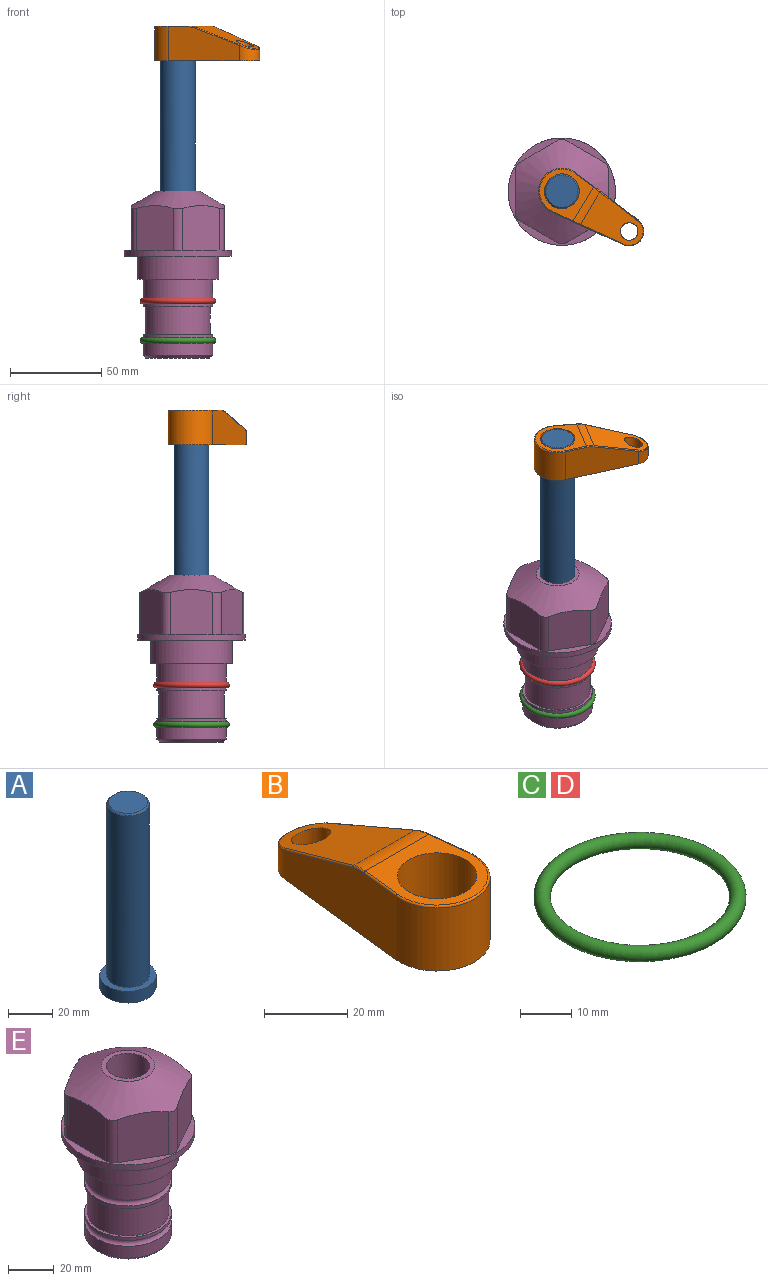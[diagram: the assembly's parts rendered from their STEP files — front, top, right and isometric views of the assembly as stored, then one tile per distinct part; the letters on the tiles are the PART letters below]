
ASSEMBLY  parts=5 mates=3
PART A: 6 faces, bbox 25.4x25.4x101.6 mm
  f0: plane 17.46x17.46mm, normal (0,0,1), area 239.5mm2, adj f5
  f1: plane 25.4x25.4mm, normal (0,0,-1), area 506.7mm2, adj f2
  f2: cylinder r=12.7mm len=25.4mm, axis (0,0,1), area 506.7mm2, adj f1,f3
  f3: plane 25.4x25.4mm, normal (0,0,1), area 221.7mm2, adj f2,f4
  f4: cylinder r=9.53mm len=94.46mm, axis (0,0,1), area 5653mm2, adj f3,f5
  f5: cone r=8.73mm half-angle=45deg, axis (0,0,-1), area 64.4mm2, adj f0,f4
PART B: 44 faces, bbox 27.5x64.5x19.1 mm
  f0: plane 2.3x0.95mm, normal (0,0,-1), area 1mm2, adj f25,f30,f34
  f1: plane 63.5x25.4mm, normal (0,0,-1), area 561.7mm2, adj f2,f3,f4,f5,f6,f7,f19,f20
  f2: cylinder r=12.7mm len=25.4mm, axis (0,0,-1), area 792.2mm2, adj f1,f3,f5,f13
  f3: plane 42.33x18.54mm, normal (0.99,0.11,0), area 647mm2, adj f1,f2,f4,f11,f12,f14
  f4: cylinder r=7.94mm len=15.78mm, axis (0,0,-1), area 158.6mm2, adj f1,f3,f5,f16
  f5: plane 42.33x18.54mm, normal (-0.99,0.11,0), area 647mm2, adj f1,f2,f4,f15,f17,f18
  f6: cylinder r=9.53mm len=19.05mm, axis (0,0,-1), area 1140.1mm2, adj f1,f8
  f7: cylinder r=4.76mm len=10.98mm, axis (0,0,-1), area 276.1mm2, adj f1,f9
  f8: plane 25.83x24.38mm, normal (0,0,1), area 262.2mm2, adj f6,f10,f11,f13,f15
  f9: plane 32.49x20.55mm, normal (0,0.34,0.94), area 489.9mm2, adj f7,f10,f14,f16,f18
  f10: cylinder r=12.7mm len=21.49mm, axis (-1,0,0), area 93.2mm2, adj f8,f9,f12,f17
  f11: cylinder r=0.51mm len=12.34mm, axis (0.11,-0.99,0), area 9.9mm2, adj f3,f8,f12,f13
  f12: bspline ~7.62x1.64mm, area 3.5mm2, adj f3,f10,f11,f14
  f13: torus R=12.19mm, axis (0,0,1), area 33.6mm2, adj f2,f8,f11,f15
  f14: cylinder r=0.51mm len=26.01mm, axis (0.1,-0.93,0.34), area 21.6mm2, adj f3,f9,f12,f16
  f15: cylinder r=0.51mm len=12.34mm, axis (0.11,0.99,0), area 9.9mm2, adj f5,f8,f13,f17
  f16: bspline ~15.78x7.05mm, area 15.7mm2, adj f4,f9,f14,f18
  f17: bspline ~7.62x1.64mm, area 3.5mm2, adj f5,f10,f15,f18
  f18: cylinder r=0.51mm len=26.01mm, axis (0.1,0.93,-0.34), area 21.6mm2, adj f5,f9,f16,f17
  f19: plane 21.6x14.29mm, normal (-0.99,-0.11,0), area 242.6mm2, adj f1,f26,f28,f34,f36,f38
  f20: plane 21.6x14.29mm, normal (0.99,-0.11,0), area 242.6mm2, adj f1,f27,f29,f37,f39,f41
  f21: cylinder r=12.7mm len=14.29mm, axis (0,0,-1), area 173.2mm2, adj f1,f26,f27,f30,f31,f33
  f22: cylinder r=7.94mm len=7.63mm, axis (0,0,-1), area 53.8mm2, adj f1,f28,f29,f42
  f23: plane 2.3x0.95mm, normal (0,0,-1), area 1mm2, adj f25,f33,f37
  f24: plane 17.94x12.32mm, normal (0,-0.34,-0.94), area 191.2mm2, adj f25,f38,f41,f42
  f25: cylinder r=9.53mm len=12.93mm, axis (-1,0,0), area 37.5mm2, adj f0,f23,f24,f31,f36,f39
  f26: cylinder r=1.59mm len=14.29mm, axis (0,0,-1), area 49mm2, adj f1,f19,f21,f32
  f27: cylinder r=1.59mm len=14.29mm, axis (0,0,-1), area 49mm2, adj f1,f20,f21,f35
  f28: cylinder r=1.59mm len=7.28mm, axis (0,0,-1), area 22.1mm2, adj f1,f19,f22,f40
  f29: cylinder r=1.59mm len=7.28mm, axis (0,0,-1), area 22.1mm2, adj f1,f20,f22,f43
  f30: torus R=14.29mm, axis (0,0,1), area 5.8mm2, adj f0,f21,f31,f32
  f31: bspline ~11.06x2.73mm, area 20.8mm2, adj f21,f25,f30,f33
  f32: sphere r=1.59mm, area 5.4mm2, adj f26,f30,f34
  f33: torus R=14.29mm, axis (0,0,1), area 5.8mm2, adj f21,f23,f31,f35
  f34: cylinder r=1.59mm len=1.68mm, axis (-0.11,0.99,0), area 2.4mm2, adj f0,f19,f32,f36
  f35: sphere r=1.59mm, area 5.4mm2, adj f27,f33,f37
  f36: bspline ~5.82x2.33mm, area 7.7mm2, adj f19,f25,f34,f38
  f37: cylinder r=1.59mm len=1.68mm, axis (0.11,0.99,0), area 2.4mm2, adj f20,f23,f35,f39
  f38: cylinder r=1.59mm len=18.33mm, axis (0.1,-0.93,0.34), area 46.7mm2, adj f19,f24,f36,f40
  f39: bspline ~5.82x2.33mm, area 7.7mm2, adj f20,f25,f37,f41
  f40: sphere r=1.59mm, area 3.6mm2, adj f28,f38,f42
  f41: cylinder r=1.59mm len=18.33mm, axis (0.1,0.93,-0.34), area 46.7mm2, adj f20,f24,f39,f43
  f42: bspline ~8.31x1.84mm, area 15.3mm2, adj f22,f24,f40,f43
  f43: sphere r=1.59mm, area 3.6mm2, adj f29,f41,f42
PART C: 1 faces, bbox 44.7x44.7x3.2 mm
  f0: torus R=19.05mm, axis (0,0,1), area 1193.9mm2
PART D: same geometry as C
PART E: 36 faces, bbox 58.7x58.7x91.2 mm
  f0: cylinder r=17.78mm len=35.56mm, axis (0,0,1), area 1670.8mm2, adj f23,f24,f31
  f1: cylinder r=19.05mm len=38.1mm, axis (0,0,1), area 1191.9mm2, adj f26,f27,f30
  f2: plane 58.66x58.66mm, normal (0,0,-1), area 1150.6mm2, adj f3,f28
  f3: cylinder r=29.33mm len=58.66mm, axis (0,0,-1), area 585.1mm2, adj f2,f4
  f4: plane 58.66x58.66mm, normal (0,0,1), area 475.9mm2, adj f3,f5,f6,f7,f8,f9,f10,f11
  f5: plane 24.5x20.32mm, normal (-0.5,0.87,0), area 562.8mm2, adj f4,f15,f16,f17
  f6: plane 24.5x20.32mm, normal (0.5,0.87,0), area 562.8mm2, adj f4,f14,f15,f17
  f7: plane 24.5x23.48mm, normal (1,0,0), area 562.8mm2, adj f4,f13,f14,f17
  f8: plane 24.5x20.32mm, normal (0.5,-0.87,0), area 562.8mm2, adj f4,f12,f13,f17
  f9: plane 24.5x20.32mm, normal (-0.5,-0.87,0), area 562.8mm2, adj f4,f11,f12,f17
  f10: plane 24.5x23.48mm, normal (-1,0,0), area 562.8mm2, adj f4,f11,f16,f17
  f11: cylinder r=5.08mm len=23.01mm, axis (0,0,-1), area 121.2mm2, adj f4,f9,f10,f17
  f12: cylinder r=5.08mm len=23.01mm, axis (0,0,-1), area 121.2mm2, adj f4,f8,f9,f17
  f13: cylinder r=5.08mm len=23.01mm, axis (0,0,-1), area 121.2mm2, adj f4,f7,f8,f17
  f14: cylinder r=5.08mm len=23.01mm, axis (0,0,-1), area 121.2mm2, adj f4,f6,f7,f17
  f15: cylinder r=5.08mm len=23.01mm, axis (0,0,-1), area 121.2mm2, adj f4,f5,f6,f17
  f16: cylinder r=5.08mm len=23.01mm, axis (0,0,-1), area 121.2mm2, adj f4,f5,f10,f17
  f17: cone r=11.73mm half-angle=60deg, axis (0,0,-1), area 2071.8mm2, adj f5,f6,f7,f8,f9,f10,f11,f12
  f18: plane 23.46x23.46mm, normal (0,0,1), area 147.4mm2, adj f17,f35
  f19: plane 34.93x34.93mm, normal (0,0,-1), area 958mm2, adj f29
  f20: cylinder r=19.05mm len=38.1mm, axis (0,0,1), area 760.1mm2, adj f21,f29
  f21: torus R=19.05mm, axis (0,0,1), area 565.3mm2, adj f20,f22
  f22: cylinder r=19.05mm len=38.1mm, axis (0,0,1), area 190mm2, adj f21,f23
  f23: plane 38.1x38.1mm, normal (0,0,1), area 146.9mm2, adj f0,f22
  f24: plane 38.1x38.1mm, normal (0,0,-1), area 146.9mm2, adj f0,f25
  f25: cylinder r=19.05mm len=38.1mm, axis (0,0,1), area 190mm2, adj f24,f26
  f26: torus R=19.05mm, axis (0,0,1), area 565.3mm2, adj f1,f25
  f27: plane 44.45x44.45mm, normal (0,0,-1), area 411.7mm2, adj f1,f28
  f28: cylinder r=22.23mm len=44.45mm, axis (0,0,1), area 1773.5mm2, adj f2,f27
  f29: cone r=19.05mm half-angle=45deg, axis (0,0,1), area 257.5mm2, adj f19,f20
  f30: cylinder r=3.17mm len=6.75mm, axis (-1,0,0), area 128mm2, adj f1,f33
  f31: cylinder r=3.17mm len=6.35mm, axis (-1,0,0), area 102.5mm2, adj f0,f33
  f32: plane 25.4x25.4mm, normal (0,0,1), area 506.7mm2, adj f33
  f33: cylinder r=12.7mm len=66.42mm, axis (0,0,-1), area 5236.2mm2, adj f30,f31,f32,f34
  f34: cone r=9.53mm half-angle=30deg, axis (0,0,-1), area 443.4mm2, adj f33,f35
  f35: cylinder r=9.53mm len=19.05mm, axis (0,0,-1), area 849mm2, adj f18,f34
PLACE A rot(axis=(0,0,-1),30.8deg) t=(0,0,52.18)mm
PLACE B rot(axis=(0,0,-1),120.8deg) t=(0,0,106.79)mm
PLACE C t=(0,0,-21.59)mm
PLACE D at identity
PLACE E at identity fixed
MATE fastened C.f0 <-> E.f0  axis (0,0,1) through (0,0,-46.1)mm
MATE cylindrical A.f2 <-> E.f0  axis (0,0,1) through (0,0,77.82)mm
MATE fastened B.f2 <-> A.f2  axis (0,0,1) through (0,0,125.84)mm
